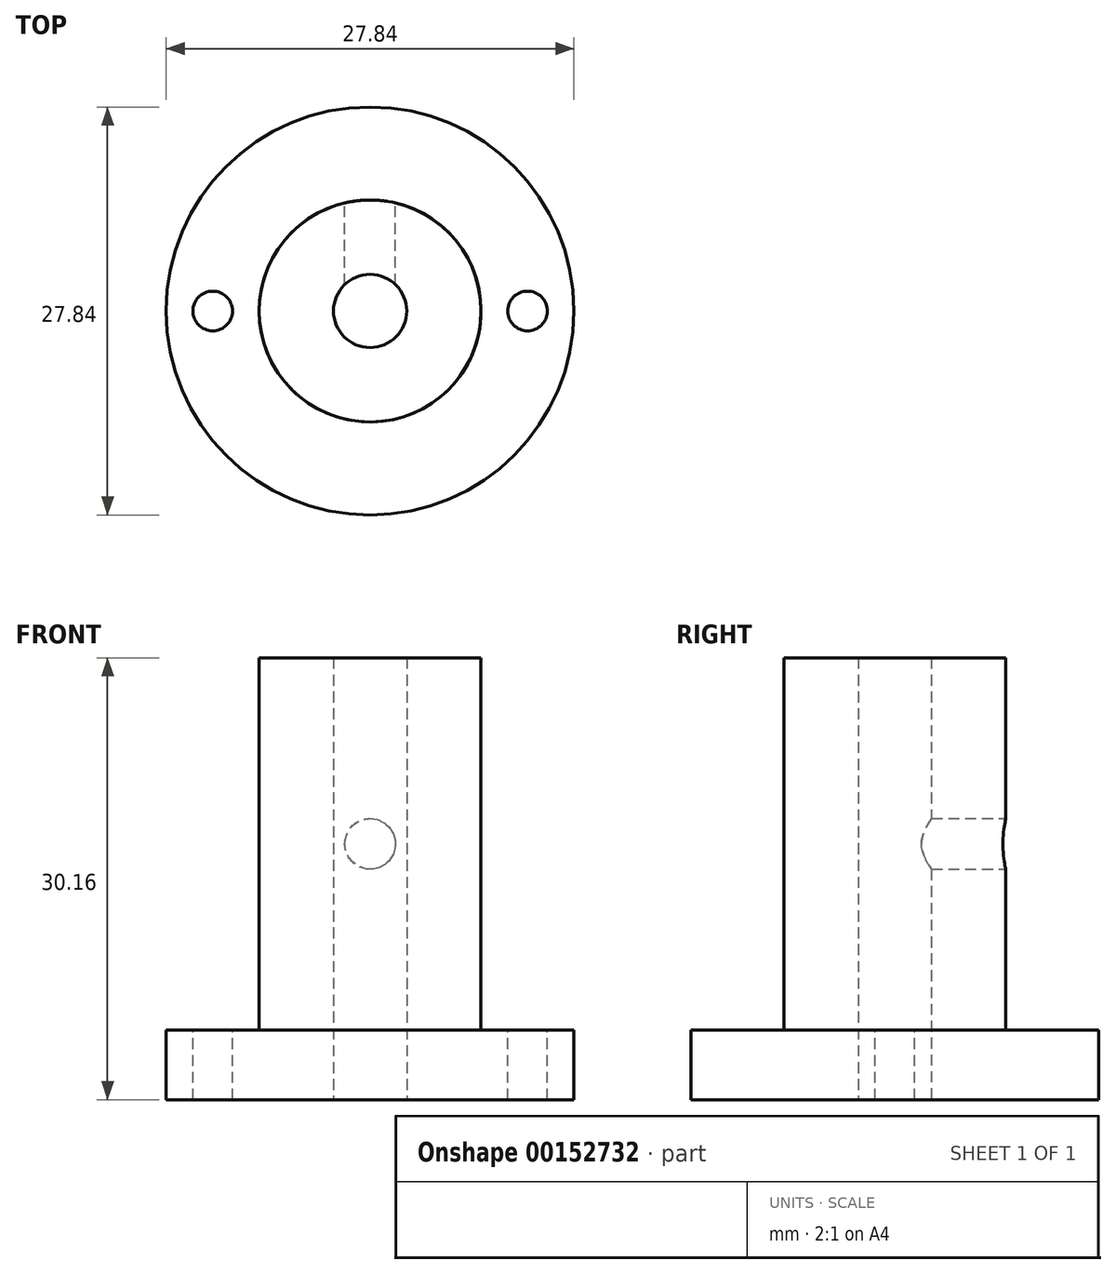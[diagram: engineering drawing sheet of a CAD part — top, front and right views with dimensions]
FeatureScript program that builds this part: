
annotation { "Feature Type Name" : "Feature", "Feature Type Description" : "" }
export const myFeature = defineFeature(function(context is Context, id is Id, definition is map)
    precondition{}
    {
        {
            var Q0;
            Q0=qCreatedBy(makeId("Top.planeOp"),FACE);
            var sketch = newSketch(context, id + "F0", { "sketchPlane" : qUnion([Q0])});
            skCircle(sketch, "E0", {"center": v(0, 0) * mm, "radius": 7.57 * mm, "construction": true});
            skLineSegment(sketch, "E1.bottom", {"start": v(7.57, 7.57) * mm, "end": v(-7.57, 7.57) * mm});
            skLineSegment(sketch, "E1.top", {"start": v(7.57, -7.57) * mm, "end": v(-7.57, -7.57) * mm});
            skLineSegment(sketch, "E1.left", {"start": v(7.57, 7.57) * mm, "end": v(7.57, -7.57) * mm});
            skLineSegment(sketch, "E1.right", {"start": v(-7.57, 7.57) * mm, "end": v(-7.57, -7.57) * mm});
            skCircle(sketch, "E2", {"center": v(0, 0) * mm, "radius": 2.5 * mm});
            skLineSegment(sketch, "E3", {"start": v(0, 0) * mm, "end": v(2.5, 0) * mm, "construction": true});
            skLineSegment(sketch, "E4.bottom", {"start": v(2.5, 2.15) * mm, "end": v(7.26, 2.15) * mm, "construction": true});
            skLineSegment(sketch, "E4.top", {"start": v(2.5, -2.15) * mm, "end": v(7.26, -2.15) * mm, "construction": true});
            skLineSegment(sketch, "E4.left", {"start": v(2.5, 2.15) * mm, "end": v(2.5, -2.15) * mm, "construction": true});
            skLineSegment(sketch, "E4.right", {"start": v(7.26, 2.15) * mm, "end": v(7.26, -2.15) * mm, "construction": true});
            skSolve(sketch);
        }
        {
            var Q0;
            Q0 = qSketchRegion(id + "F0", true);
            extrude(context, id + "F1", {"entities" : qUnion([Q0]), "depth" : 25.4 * mm});
        }
        {
            var Q0;
            Q0=makeQuery(id+"F1.opExtrude","SWEPT_FACE",FACE,{"disambiguationData":[OSD([sQuery(id+"F0.wireOp",EDGE,"E1.bottom")])]});
            var sketch = newSketch(context, id + "F2", { "sketchPlane" : qUnion([Q0])});
            skLineSegment(sketch, "E5", {"start": v(0, 25.4) * mm, "end": v(0, 0) * mm, "construction": true});
            skCircle(sketch, "E6", {"center": v(0, 12.7) * mm, "radius": 1.73 * mm});
            skSolve(sketch);
        }
        {
            var Q0;
            Q0 = qSketchRegion(id + "F2", true);
            var Q1;
            Q1=makeQuery(id+"F1.opExtrude","SWEPT_FACE",FACE,{"disambiguationData":[OSD([sQuery(id+"F0.wireOp",EDGE,"E2")])]});
            extrude(context, id + "F3", {"entities" : qUnion([Q0]), "operationType" : NewBodyOperationType.REMOVE, "endBound" : BoundingType.UP_TO_SURFACE, "oppositeDirection" : true, "endBoundEntityFace" : qUnion([Q1]), "depth" : 25.4 * mm});
        }
        {
            var Q0;
            Q0=makeQuery(id+"F1.opExtrude","CAP_FACE",FACE,{"disambiguationData":[OSD([sQuery(id+"F0.wireOp",EDGE,"E1.bottom"),sQuery(id+"F0.wireOp",EDGE,"E1.top"),sQuery(id+"F0.wireOp",EDGE,"E1.left"),sQuery(id+"F0.wireOp",EDGE,"E1.right"),sQuery(id+"F0.wireOp",EDGE,"E2")])],"isStart":true});
            var sketch = newSketch(context, id + "F4", { "sketchPlane" : qUnion([Q0])});
            skCircle(sketch, "E7", {"center": v(0, 0) * mm, "radius": 2.5 * mm});
            skCircle(sketch, "E8", {"center": v(0, 0) * mm, "radius": 13.92 * mm});
            skLineSegment(sketch, "E9", {"start": v(10.75, 0) * mm, "end": v(-10.75, 0) * mm, "construction": true});
            skCircle(sketch, "E10", {"center": v(10.75, 0) * mm, "radius": 3.18 * mm, "construction": true});
            skCircle(sketch, "E11", {"center": v(10.75, 0) * mm, "radius": 1.35 * mm});
            skCircle(sketch, "E12", {"center": v(-10.75, 0) * mm, "radius": 1.35 * mm});
            skSolve(sketch);
        }
        {
            var Q0;
            Q0 = qSketchRegion(id + "F4", true);
            extrude(context, id + "F5", {"entities" : qUnion([Q0]), "operationType" : NewBodyOperationType.ADD, "depth" : 4.76 * mm});
        }
        {
            var Q0;
            Q0=makeQuery(id+"F1.opExtrude","SWEPT_EDGE",EDGE,{"disambiguationData":[OSD([sQuery(id+"F0.wireOp",EDGE,"E1.bottom"),sQuery(id+"F0.wireOp",EDGE,"E1.right")])]});
            var Q1;
            Q1=makeQuery(id+"F1.opExtrude","SWEPT_EDGE",EDGE,{"disambiguationData":[OSD([sQuery(id+"F0.wireOp",EDGE,"E1.bottom"),sQuery(id+"F0.wireOp",EDGE,"E1.left")])]});
            var Q2;
            Q2=makeQuery(id+"F1.opExtrude","SWEPT_EDGE",EDGE,{"disambiguationData":[OSD([sQuery(id+"F0.wireOp",EDGE,"E1.top"),sQuery(id+"F0.wireOp",EDGE,"E1.right")])]});
            var Q3;
            Q3=makeQuery(id+"F1.opExtrude","SWEPT_EDGE",EDGE,{"disambiguationData":[OSD([sQuery(id+"F0.wireOp",EDGE,"E1.top"),sQuery(id+"F0.wireOp",EDGE,"E1.left")])]});
            fillet(context, id + "F6", {"entities" : qUnion([Q0, Q1, Q2, Q3]), "radius" : 7.57 * mm, "tangentPropagation" : true, "allowEdgeOverflow" : false});
        }
    });
